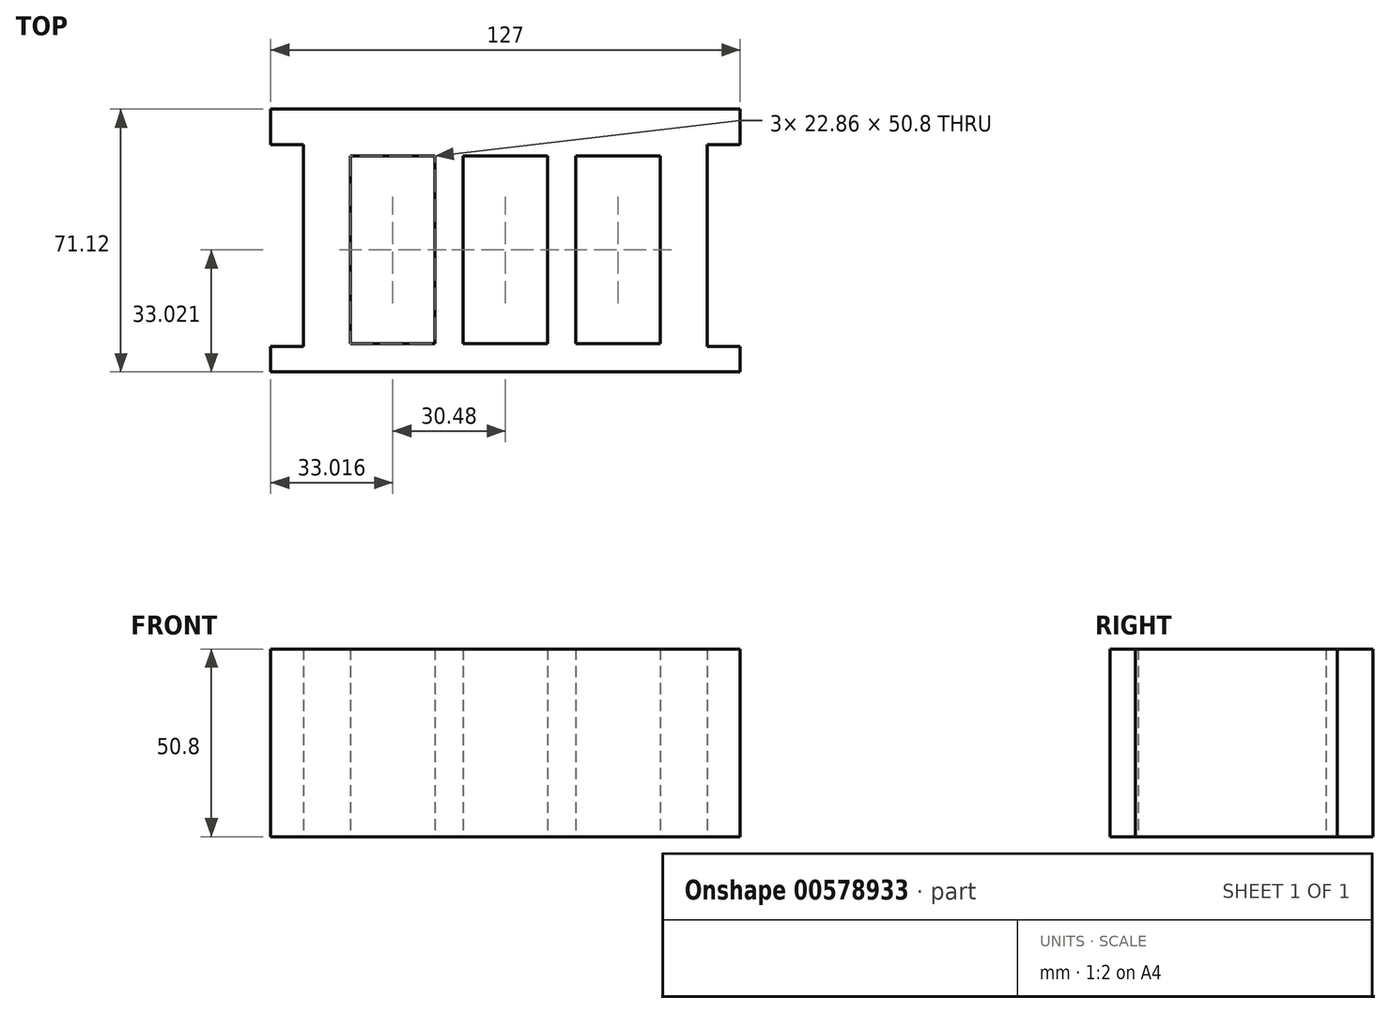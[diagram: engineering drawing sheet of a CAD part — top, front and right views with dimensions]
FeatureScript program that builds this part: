
annotation { "Feature Type Name" : "Feature", "Feature Type Description" : "" }
export const myFeature = defineFeature(function(context is Context, id is Id, definition is map)
    precondition{}
    {
        {
            var Q0;
            Q0=qCreatedBy(makeId("Top.planeOp"),FACE);
            var sketch = newSketch(context, id + "F0", { "sketchPlane" : qUnion([Q0])});
            skLineSegment(sketch, "E0", {"start": v(-6.6, 42.17) * mm, "end": v(56.9, 42.17) * mm});
            skLineSegment(sketch, "E1", {"start": v(56.9, 42.17) * mm, "end": v(56.9, 32.53) * mm});
            skLineSegment(sketch, "E2", {"start": v(56.9, 32.53) * mm, "end": v(48, 32.53) * mm});
            skLineSegment(sketch, "E3", {"start": v(48, 32.53) * mm, "end": v(48, -22.08) * mm});
            skLineSegment(sketch, "E4", {"start": v(48, -22.08) * mm, "end": v(56.9, -22.08) * mm});
            skLineSegment(sketch, "E5", {"start": v(56.9, -22.08) * mm, "end": v(56.9, -28.95) * mm});
            skLineSegment(sketch, "E6", {"start": v(56.9, -28.95) * mm, "end": v(-70.1, -28.95) * mm});
            skLineSegment(sketch, "E7", {"start": v(-70.1, -28.95) * mm, "end": v(-70.1, -22.08) * mm});
            skLineSegment(sketch, "E8", {"start": v(-70.1, -22.08) * mm, "end": v(-61.21, -22.08) * mm});
            skLineSegment(sketch, "E9", {"start": v(-61.21, -22.08) * mm, "end": v(-61.21, 32.53) * mm});
            skLineSegment(sketch, "E10", {"start": v(-61.21, 32.53) * mm, "end": v(-70.1, 32.53) * mm});
            skLineSegment(sketch, "E11", {"start": v(-70.1, 32.53) * mm, "end": v(-70.1, 42.17) * mm});
            skLineSegment(sketch, "E12", {"start": v(-70.1, 42.17) * mm, "end": v(-6.6, 42.17) * mm});
            skLineSegment(sketch, "E13.bottom", {"start": v(-48.51, 29.47) * mm, "end": v(-25.65, 29.47) * mm});
            skLineSegment(sketch, "E13.top", {"start": v(-48.51, -21.33) * mm, "end": v(-25.65, -21.33) * mm});
            skLineSegment(sketch, "E13.left", {"start": v(-48.51, 29.47) * mm, "end": v(-48.51, -21.33) * mm});
            skLineSegment(sketch, "E13.right", {"start": v(-25.65, 29.47) * mm, "end": v(-25.65, -21.33) * mm});
            skLineSegment(sketch, "E14.bottom", {"start": v(-18.03, 29.47) * mm, "end": v(4.83, 29.47) * mm});
            skLineSegment(sketch, "E14.top", {"start": v(-18.03, -21.33) * mm, "end": v(4.83, -21.33) * mm});
            skLineSegment(sketch, "E14.left", {"start": v(-18.03, 29.47) * mm, "end": v(-18.03, -21.33) * mm});
            skLineSegment(sketch, "E14.right", {"start": v(4.83, 29.47) * mm, "end": v(4.83, -21.33) * mm});
            skLineSegment(sketch, "E15.bottom", {"start": v(12.45, 29.47) * mm, "end": v(35.3, 29.47) * mm});
            skLineSegment(sketch, "E15.top", {"start": v(12.45, -21.33) * mm, "end": v(35.3, -21.33) * mm});
            skLineSegment(sketch, "E15.left", {"start": v(12.45, 29.47) * mm, "end": v(12.45, -21.33) * mm});
            skLineSegment(sketch, "E15.right", {"start": v(35.3, 29.47) * mm, "end": v(35.3, -21.33) * mm});
            skSolve(sketch);
        }
        {
            var Q0;
            Q0=makeQuery(id+"F0.imprint","IMPRINT",FACE,{"disambiguationData":[TD([[makeQuery(id+"F0.imprint","IMPRINT",EDGE,{"derivedFrom":sQuery(id+"F0.wireOp",EDGE,"E0")}),-1.0]])]});
            extrude(context, id + "F1", {"entities" : qUnion([Q0]), "depth" : 50.8 * mm, "offsetDistance" : 25.4 * mm});
        }
    });
